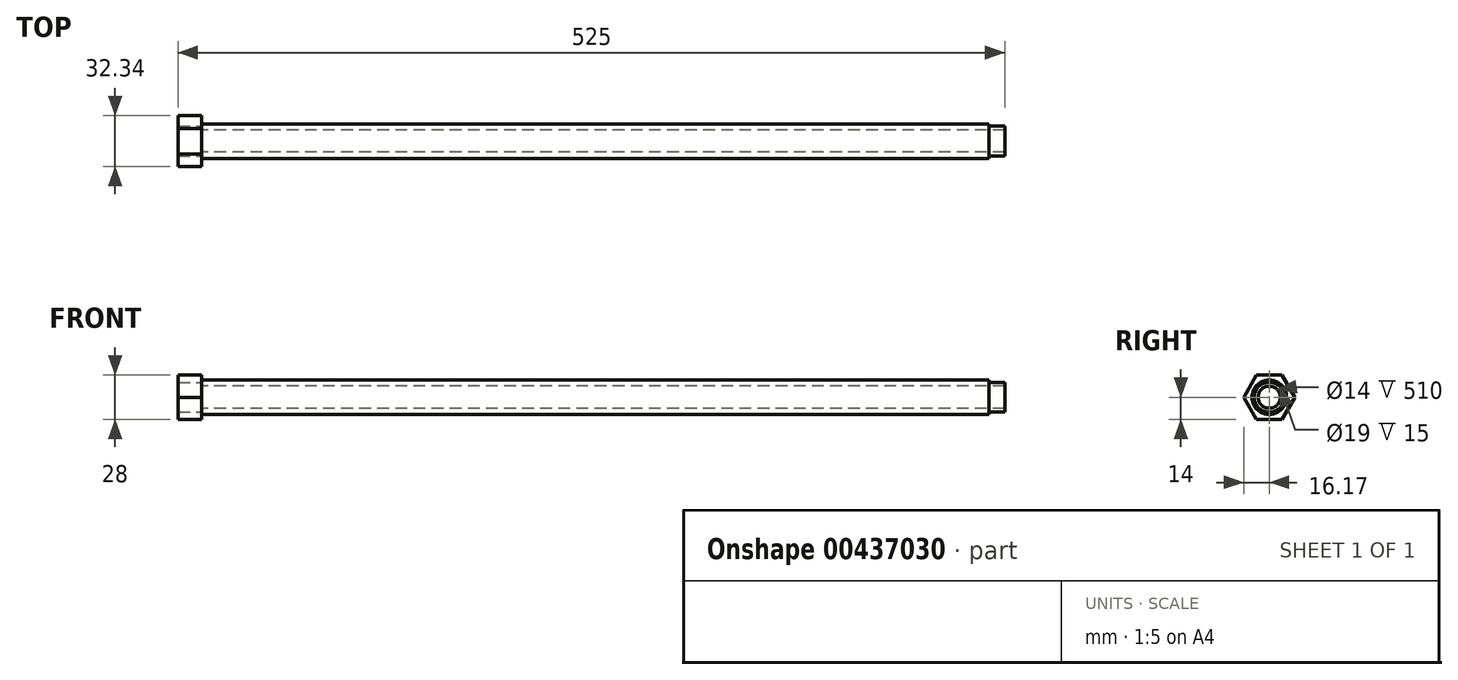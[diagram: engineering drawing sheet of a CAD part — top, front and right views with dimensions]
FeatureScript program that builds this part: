
annotation { "Feature Type Name" : "Feature", "Feature Type Description" : "" }
export const myFeature = defineFeature(function(context is Context, id is Id, definition is map)
    precondition{}
    {
        {
            var Q0;
            Q0=qCreatedBy(makeId("Right.planeOp"),FACE);
            var sketch = newSketch(context, id + "F0", { "sketchPlane" : qUnion([Q0])});
            skCircle(sketch, "E0", {"center": v(0, 0) * mm, "radius": 11 * mm});
            skCircle(sketch, "E1", {"center": v(0, 0) * mm, "radius": 7 * mm});
            skSolve(sketch);
        }
        {
            var Q0;
            Q0=qSketchRegion(id+"F0",true);
            extrude(context, id + "F1", {"entities" : qUnion([Q0]), "depth" : 500 * mm});
        }
        {
            var Q0;
            Q0=makeQuery(id+"F1.opExtrude","CAP_FACE",FACE,{"disambiguationData":[OSD([sQuery(id+"F0.wireOp",EDGE,"E0"),sQuery(id+"F0.wireOp",EDGE,"E1")])],"isStart":false});
            var sketch = newSketch(context, id + "F2", { "sketchPlane" : qUnion([Q0])});
            skCircle(sketch, "E2", {"center": v(0, 0) * mm, "radius": 7 * mm});
            skCircle(sketch, "E3", {"center": v(0, 0) * mm, "radius": 9.5 * mm});
            skSolve(sketch);
        }
        {
            var Q0;
            Q0=qSketchRegion(id+"F2",true);
            extrude(context, id + "F3", {"entities" : qUnion([Q0]), "operationType" : NewBodyOperationType.ADD, "depth" : 10 * mm});
        }
        {
            var Q0;
            Q0=makeQuery(id+"F1.opExtrude","CAP_FACE",FACE,{"disambiguationData":[OSD([sQuery(id+"F0.wireOp",EDGE,"E0"),sQuery(id+"F0.wireOp",EDGE,"E1")])],"isStart":true});
            var sketch = newSketch(context, id + "F4", { "sketchPlane" : qUnion([Q0])});
            skCircle(sketch, "E4", {"center": v(0, 0) * mm, "radius": 9.5 * mm});
            skCircle(sketch, "E5", {"center": v(0, 0) * mm, "radius": 14 * mm});
            skCircle(sketch, "E6.cCircle", {"center": v(0, 0) * mm, "radius": 14 * mm, "construction": true});
            skLineSegment(sketch, "E6.0", {"start": v(-8.08, 14) * mm, "end": v(8.08, 14) * mm});
            skLineSegment(sketch, "E6.1", {"start": v(8.08, 14) * mm, "end": v(16.17, 0) * mm});
            skLineSegment(sketch, "E6.2", {"start": v(16.17, 0) * mm, "end": v(8.08, -14) * mm});
            skLineSegment(sketch, "E6.3", {"start": v(8.08, -14) * mm, "end": v(-8.08, -14) * mm});
            skLineSegment(sketch, "E6.4", {"start": v(-8.08, -14) * mm, "end": v(-16.17, 0) * mm});
            skLineSegment(sketch, "E6.5", {"start": v(-16.17, 0) * mm, "end": v(-8.08, 14) * mm});
            skPoint(sketch, "E6.0.midPoint", {"position": v(0, 14) * mm});
            skSolve(sketch);
        }
        {
            var Q0;
            Q0=qSketchRegion(id+"F4",true);
            extrude(context, id + "F5", {"entities" : qUnion([Q0]), "operationType" : NewBodyOperationType.ADD, "depth" : 15 * mm});
        }
    });
